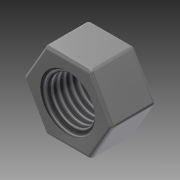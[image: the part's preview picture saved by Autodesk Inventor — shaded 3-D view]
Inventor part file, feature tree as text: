
AUTODESK INVENTOR PART (.ipt)
format: ipt  version: 2013 (Build 170138000, 138)  size: 153,088 bytes
history: native  units: mm
features: thread x3, other x1, extrude x1, fillet x1, chamfer x1, sketch x1
ambient origin geometry x8: Origin, YZ Plane, XZ Plane, XY Plane, X Axis, Y Axis, Z Axis, Center Point
feature tree (8):
  other  "Sólido1"
  extrude  "Extrusión1"  Depth=7.0mm
  thread  "Rosca1"  [1 undecoded]
  fillet  "Empalme1"  Radius=7.0mm
  chamfer  "Chaflán1"  Distance=7.0mm
  thread  "Rosca2"  [1 undecoded]
  thread  "Rosca3"  [1 undecoded]
  sketch  "Boceto1"  dims[d21=7.0mm d22=7.0mm d23=120.0deg d24=7.0mm d25=7.0mm d26=7.0mm d27=120.0deg d28=7.0mm d29=7.0mm d30=0.0mm d31=10.0mm d32=0.0mm d33=0.5mm d34=0.8mm d35=2.0mm d36=45.0deg d37=10.0mm d38=0.0mm d39=10.0mm d40=0.0mm]
note: 3 required parameter values undecoded (feature->parameter linkage not recoverable at this tier; creation-order binding heuristic only, values carry confidence <= 0.55)
